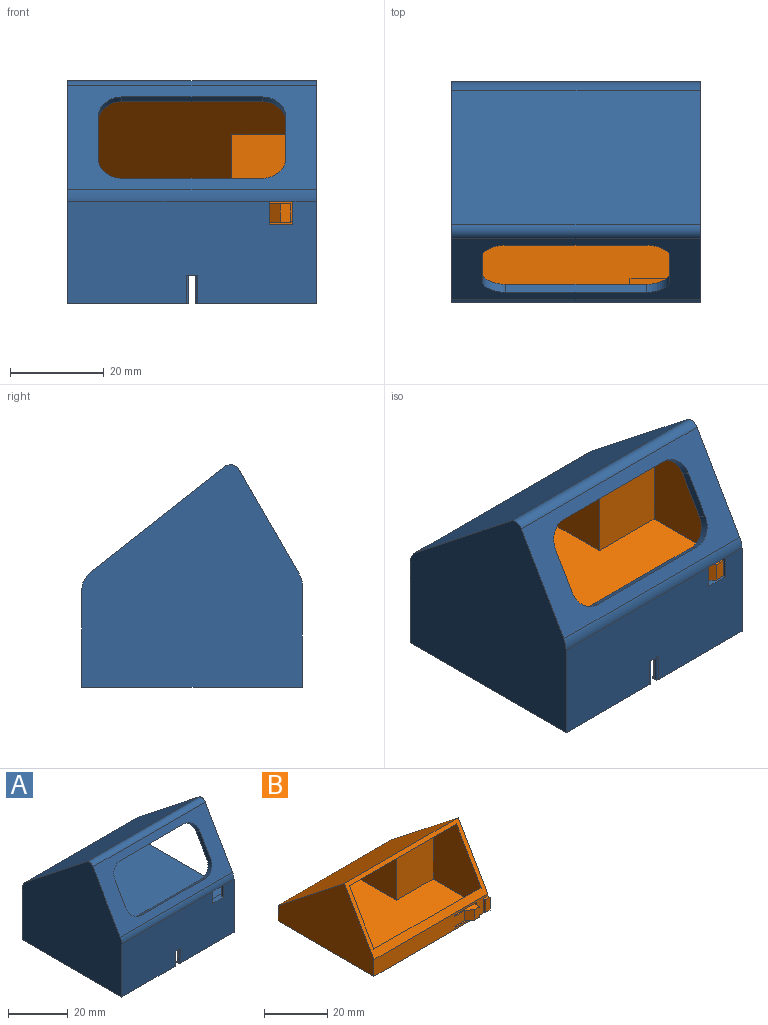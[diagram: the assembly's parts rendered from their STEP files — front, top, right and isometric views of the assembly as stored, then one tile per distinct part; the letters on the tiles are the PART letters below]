
ASSEMBLY  parts=2 mates=1
PART A: 49 faces, bbox 53x47x47.4 mm
  f0: plane 47x25.75mm, normal (0,0,-1), area 143mm2, adj f2,f3,f7,f8,f9,f31,f37,f38
  f1: plane 47x25.75mm, normal (0,0,-1), area 143mm2, adj f2,f3,f6,f7,f8,f32,f34,f35
  f2: plane 50x12mm, normal (0,1,0), area 585mm2, adj f0,f1,f31,f32,f33,f41,f46,f47
  f3: plane 50x12mm, normal (0,-1,0), area 585mm2, adj f0,f1,f31,f32,f33,f36,f37,f40
  f4: plane 53x22.28mm, normal (0,-0.87,0.5), area 584.9mm2, adj f6,f9,f20,f21,f23,f24,f25,f26
  f5: plane 51x22.97mm, normal (0,0.87,-0.5), area 574.4mm2, adj f9,f12,f13,f15,f23,f24,f25,f26
  f6: plane 47.44x47mm, normal (-1,0,0), area 1676.6mm2, adj f1,f4,f7,f8,f10,f20,f21,f22
  f7: plane 53x20.57mm, normal (0,1,0), area 1075.4mm2, adj f0,f1,f6,f9,f22,f34,f39,f40
  f8: plane 53x21.66mm, normal (0,-1,0), area 1108.4mm2, adj f0,f1,f6,f9,f16,f17,f18,f21
  f9: plane 47.44x47mm, normal (1,0,0), area 906.2mm2, adj f0,f4,f5,f7,f8,f10,f11,f12
  f10: plane 53x28.59mm, normal (0,0.62,0.79), area 1928.6mm2, adj f6,f9,f20,f22
  f11: plane 51x6.03mm, normal (0,-1,0), area 307.5mm2, adj f9,f12,f14,f15
  f12: plane 51x29.74mm, normal (0,-0.62,-0.79), area 1930.1mm2, adj f5,f9,f11,f15
  f13: plane 51x6.46mm, normal (0,1,0), area 279.7mm2, adj f5,f9,f14,f15,f17,f18,f19
  f14: plane 51x43mm, normal (0,0,1), area 2193mm2, adj f9,f11,f13,f15
  f15: plane 43x29.44mm, normal (1,0,0), area 765.4mm2, adj f5,f11,f12,f13,f14
  f16: plane 5x1mm, normal (-1,0,0), area 5mm2, adj f8,f17,f19,f21,f48
  f17: plane 10x2mm, normal (0,0,1), area 15mm2, adj f8,f9,f13,f16,f18,f48
  f18: plane 5x2mm, normal (1,0,0), area 10mm2, adj f8,f13,f17,f19,f21
  f19: plane 10x2mm, normal (0,0,-1), area 15mm2, adj f9,f13,f16,f18,f21,f48
  f20: cylinder r=2mm len=53mm, axis (1,0,0), area 181.7mm2, adj f4,f6,f9,f10
  f21: cylinder r=5mm len=53mm, axis (1,0,0), area 138.4mm2, adj f4,f6,f8,f9,f16,f18,f19
  f22: cylinder r=5mm len=53mm, axis (-1,0,0), area 239.5mm2, adj f6,f7,f9,f10
  f23: plane 30x1.73mm, normal (0,0.5,0.87), area 60mm2, adj f4,f5,f24,f30
  f24: cylinder r=5mm len=5.33mm, axis (0,-0.87,0.5), area 15.7mm2, adj f4,f5,f23,f25
  f25: plane 9.66x6.73mm, normal (-1,0,0), area 20mm2, adj f4,f5,f24,f26
  f26: cylinder r=5mm len=5.33mm, axis (0,-0.87,0.5), area 15.7mm2, adj f4,f5,f25,f27
  f27: plane 30x1.73mm, normal (0,-0.5,-0.87), area 60mm2, adj f4,f5,f26,f28
  f28: cylinder r=5mm len=5.33mm, axis (0,-0.87,0.5), area 15.7mm2, adj f4,f5,f27,f29
  f29: plane 9.66x6.73mm, normal (1,0,0), area 20mm2, adj f4,f5,f28,f30
  f30: cylinder r=5mm len=5.33mm, axis (0,-0.87,0.5), area 15.7mm2, adj f4,f5,f23,f29
  f31: plane 44x12mm, normal (-1,0,0), area 528mm2, adj f0,f2,f3,f33
  f32: plane 44x12mm, normal (1,0,0), area 528mm2, adj f1,f2,f3,f33
  f33: plane 50x44mm, normal (0,0,-1), area 2200mm2, adj f2,f3,f31,f32
  f34: cylinder r=0.5mm len=6mm, axis (0,0,-1), area 4.7mm2, adj f1,f7,f35,f40
  f35: plane 6x0.5mm, normal (1,0,0), area 3mm2, adj f1,f34,f36,f40
  f36: cylinder r=0.5mm len=6mm, axis (0,0,-1), area 4.7mm2, adj f1,f3,f35,f40
  f37: cylinder r=0.5mm len=6mm, axis (0,0,-1), area 4.7mm2, adj f0,f3,f38,f40
  f38: plane 6x0.5mm, normal (-1,0,0), area 3mm2, adj f0,f37,f39,f40
  f39: cylinder r=0.5mm len=6mm, axis (0,0,-1), area 4.7mm2, adj f0,f7,f38,f40
  f40: plane 2.5x1.5mm, normal (0,0,-1), area 2.5mm2, adj f3,f7,f34,f35,f36,f37,f38,f39
  f41: cylinder r=0.5mm len=6mm, axis (0,0,-1), area 4.7mm2, adj f1,f2,f42,f47
  f42: plane 6x0.5mm, normal (1,0,0), area 3mm2, adj f1,f41,f43,f47
  f43: cylinder r=0.5mm len=6mm, axis (0,0,-1), area 4.7mm2, adj f1,f8,f42,f47
  f44: cylinder r=0.5mm len=6mm, axis (0,0,-1), area 4.7mm2, adj f0,f8,f45,f47
  f45: plane 6x0.5mm, normal (-1,0,0), area 3mm2, adj f0,f44,f46,f47
  f46: cylinder r=0.5mm len=6mm, axis (0,0,-1), area 4.7mm2, adj f0,f2,f45,f47
  f47: plane 2.5x1.5mm, normal (0,0,-1), area 2.5mm2, adj f2,f8,f41,f42,f43,f44,f45,f46
  f48: plane 5x5mm, normal (0,1,0), area 25mm2, adj f9,f16,f17,f19
PART B: 35 faces, bbox 51x45x29.4 mm
  f0: plane 51x6.46mm, normal (0,-1,0), area 288.7mm2, adj f1,f2,f3,f4,f9,f12,f23,f24
  f1: plane 9.5x3mm, normal (0,0,-1), area 16.5mm2, adj f0,f2,f26,f28,f29,f30
  f2: plane 5x3mm, normal (1,0,0), area 4.7mm2, adj f0,f1,f5,f13,f22,f23,f25,f27
  f3: plane 51x43mm, normal (0,0,-1), area 2193mm2, adj f0,f4,f10,f12
  f4: plane 44x29.44mm, normal (1,0,0), area 561.1mm2, adj f0,f3,f9,f10,f11,f17,f18,f19
  f5: plane 48x40mm, normal (0,0,1), area 1599.8mm2, adj f2,f6,f8,f13,f14,f15,f16,f22
  f6: plane 31.5x3.8mm, normal (0,-1,0), area 119.7mm2, adj f5,f7,f14,f16
  f7: plane 48x28.99mm, normal (0,-0.62,-0.79), area 1382.7mm2, adj f6,f8,f9,f14,f15,f16
  f8: plane 26.63x21.5mm, normal (-1,0,0), area 424.2mm2, adj f5,f7,f9,f13,f15
  f9: plane 51x22.97mm, normal (0,-0.87,0.5), area 296.3mm2, adj f0,f4,f7,f8,f11,f12,f13,f14
  f10: plane 51x6.03mm, normal (0,1,0), area 307.5mm2, adj f3,f4,f11,f12
  f11: plane 51x29.74mm, normal (0,0.62,0.79), area 1930.1mm2, adj f4,f9,f10,f12
  f12: plane 43x29.44mm, normal (-1,0,0), area 765.4mm2, adj f0,f3,f9,f10,f11
  f13: plane 48x7.56mm, normal (0,1,0), area 320.7mm2, adj f2,f5,f8,f9,f14,f23,f24
  f14: plane 40x26.63mm, normal (1,0,0), area 629.2mm2, adj f5,f6,f7,f9,f13
  f15: plane 18.36x16.5mm, normal (0,-1,0), area 303mm2, adj f5,f7,f8,f16
  f16: plane 18.5x18.36mm, normal (-1,0,0), area 205mm2, adj f5,f6,f7,f15
  f17: plane 18.71x17mm, normal (0,1,0), area 318.1mm2, adj f4,f18,f20,f21
  f18: plane 18x17mm, normal (0,0,1), area 306mm2, adj f4,f17,f19,f21
  f19: plane 17x4.54mm, normal (0,-1,0), area 77.2mm2, adj f4,f18,f20,f21
  f20: plane 18x17mm, normal (0,-0.62,-0.79), area 389.4mm2, adj f4,f17,f19,f21
  f21: plane 18.71x18mm, normal (1,0,0), area 209.3mm2, adj f17,f18,f19,f20
  f22: plane 10x0.77mm, normal (0,-1,0), area 7.7mm2, adj f2,f5,f24,f25
  f23: plane 10x1.5mm, normal (0,0,-1), area 15mm2, adj f0,f2,f13,f24
  f24: plane 5x3mm, normal (-1,0,0), area 8.7mm2, adj f0,f5,f13,f22,f23,f25
  f25: plane 10x3mm, normal (0,0,1), area 30mm2, adj f0,f2,f22,f24
  f26: plane 4x3mm, normal (1,0,0), area 12mm2, adj f1,f27,f28,f29
  f27: plane 9.5x3mm, normal (0,0,1), area 16.5mm2, adj f0,f2,f26,f28,f29,f30
  f28: plane 9.5x4mm, normal (0,1,0), area 38mm2, adj f1,f2,f26,f27
  f29: plane 4x2.25mm, normal (0,-1,0), area 9mm2, adj f1,f26,f27,f30
  f30: plane 4x2.5mm, normal (-0.62,-0.78,0), area 12.8mm2, adj f0,f1,f27,f29
  f31: plane 5x1mm, normal (-1,0,0), area 5mm2, adj f0,f32,f33,f34
  f32: plane 2x1mm, normal (0,0,-1), area 2mm2, adj f0,f4,f31,f34
  f33: plane 2x1mm, normal (0,0,1), area 2mm2, adj f0,f4,f31,f34
  f34: plane 5x2mm, normal (0,-1,0), area 10mm2, adj f4,f31,f32,f33
PLACE A t=(28.07,25.19,-16.6)mm fixed
PLACE B t=(54.57,29.92,0.25)mm
MATE slider A.f15 <-> B.f12  axis (1,0,0) through (3.57,30.82,9.57)mm
